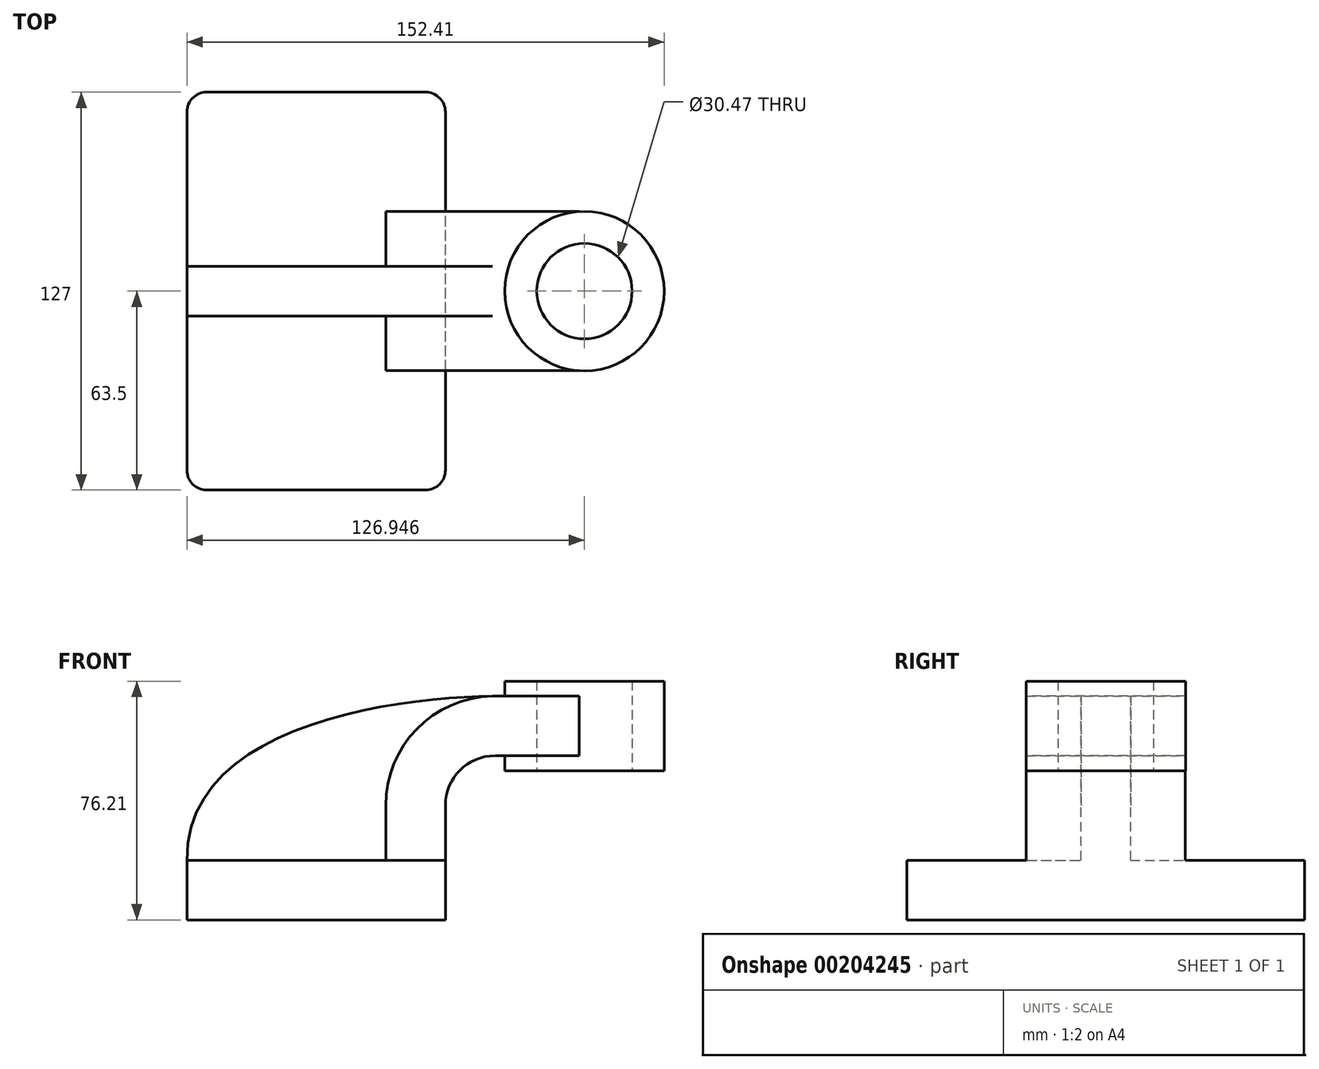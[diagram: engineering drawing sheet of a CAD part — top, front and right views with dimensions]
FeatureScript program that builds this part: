
annotation { "Feature Type Name" : "Feature", "Feature Type Description" : "" }
export const myFeature = defineFeature(function(context is Context, id is Id, definition is map)
    precondition{}
    {
        {
            var Q0;
            Q0=qCreatedBy(makeId("Front.planeOp"),FACE);
            var sketch = newSketch(context, id + "F0", { "sketchPlane" : qUnion([Q0])});
            skLineSegment(sketch, "E0.bottom", {"start": v(-41.28, -9.53) * mm, "end": v(41.28, -9.53) * mm});
            skLineSegment(sketch, "E0.top", {"start": v(-41.28, 9.53) * mm, "end": v(41.28, 9.53) * mm});
            skLineSegment(sketch, "E0.left", {"start": v(-41.28, -9.53) * mm, "end": v(-41.28, 9.53) * mm});
            skLineSegment(sketch, "E0.right", {"start": v(41.28, -9.53) * mm, "end": v(41.28, 9.52) * mm});
            skPoint(sketch, "E0.middle", {"position": v(0, 0) * mm});
            skLineSegment(sketch, "E1.bottom", {"start": v(60.33, 38.1) * mm, "end": v(111.12, 38.1) * mm});
            skLineSegment(sketch, "E1.top", {"start": v(60.33, 66.67) * mm, "end": v(111.12, 66.67) * mm});
            skLineSegment(sketch, "E1.left", {"start": v(60.33, 38.1) * mm, "end": v(60.33, 66.67) * mm});
            skLineSegment(sketch, "E1.right", {"start": v(111.12, 38.1) * mm, "end": v(111.12, 66.67) * mm});
            skPoint(sketch, "E1.middle", {"position": v(85.72, 52.39) * mm});
            skLineSegment(sketch, "E2", {"start": v(41.28, 9.53) * mm, "end": v(41.28, 27) * mm});
            skArc(sketch, "E3", {"start": v(41.27, 27) * mm, "mid": v(45.92, 38.23) * mm, "end": v(57.15, 42.88) * mm});
            skLineSegment(sketch, "E4", {"start": v(57.15, 42.88) * mm, "end": v(85.67, 42.88) * mm});
            skLineSegment(sketch, "E5.0", {"start": v(57.15, 61.93) * mm, "end": v(85.67, 61.93) * mm});
            skArc(sketch, "E5.1", {"start": v(22.23, 27) * mm, "mid": v(32.45, 51.7) * mm, "end": v(57.15, 61.93) * mm});
            skLineSegment(sketch, "E5.2", {"start": v(22.23, 9.53) * mm, "end": v(22.23, 27) * mm});
            skLineSegment(sketch, "E6", {"start": v(85.67, 66.67) * mm, "end": v(85.67, 38.1) * mm});
            skFitSpline(sketch, "E7", {"points": [v(-41.28, 9.53) * mm, v(57.15, 61.93) * mm], "startDerivative": vector(-1.17, 130.74) * mm, "endDerivative": vector(93.52, 0.92) * mm});
            skSolve(sketch);
        }
        {
            var Q0;
            Q0=makeQuery(id+"F0.imprint","IMPRINT",FACE,{"disambiguationData":[TD([[makeQuery(id+"F0.imprint","IMPRINT",EDGE,{"derivedFrom":sQuery(id+"F0.wireOp",EDGE,"E0.bottom")}),1.0]])]});
            extrude(context, id + "F1", {"entities" : qUnion([Q0]), "depth" : 127 * mm, "symmetric" : true});
        }
        {
            var Q0;
            {var subQ3=sQuery(id+"F0.wireOp",EDGE,"E5.2");Q0=makeQuery(id+"F0.imprint","IMPRINT",FACE,{"disambiguationData":[TD([[makeQuery(id+"F0.imprint","IMPRINT",EDGE,{"derivedFrom":subQ3}),1.0]])]});}
            extrude(context, id + "F2", {"entities" : qUnion([Q0]), "operationType" : NewBodyOperationType.ADD, "depth" : 15.88 * mm, "symmetric" : true});
        }
        {
            var Q0;
            {var subQ5=sQuery(id+"F0.wireOp",EDGE,"E2");Q0=makeQuery(id+"F0.imprint","IMPRINT",FACE,{"disambiguationData":[TD([[makeQuery(id+"F0.imprint","IMPRINT",EDGE,{"derivedFrom":subQ5}),1.0]])]});}
            var Q1;
            {var subQ0=sQuery(id+"F0.wireOp",EDGE,"E4");var subQ1=sQuery(id+"F0.wireOp",EDGE,"E1.left");var subQ2=makeQuery(id+"F0.imprint","INTERSECT",VERTEX,{"derivedFrom":[subQ1,subQ0]});Q1=makeQuery(id+"F0.imprint","IMPRINT",FACE,{"disambiguationData":[TD([[makeQuery(id+"F0.imprint","IMPRINT",EDGE,{"disambiguationData":[TD([[subQ2,-1.0]])],"derivedFrom":subQ1}),-1.0]])]});}
            extrude(context, id + "F3", {"entities" : qUnion([Q0, Q1]), "operationType" : NewBodyOperationType.ADD, "depth" : 50.8 * mm, "symmetric" : true});
        }
        {
            var Q0;
            {var subQ0=sQuery(id+"F0.wireOp",EDGE,"E1.right");Q0=makeQuery(id+"F0.imprint","IMPRINT",FACE,{"disambiguationData":[TD([[makeQuery(id+"F0.imprint","IMPRINT",EDGE,{"derivedFrom":subQ0}),1.0]])]});}
            var Q1;
            Q1=sQuery(id+"F0.wireOp",EDGE,"E6");
            revolve(context, id + "F4", {"operationType" : NewBodyOperationType.ADD, "entities" : qUnion([Q0]), "axis" : qUnion([Q1]), "revolveType" : RevolveType.FULL});
        }
        {
            var Q0;
            Q0=makeQuery(id+"F1.opExtrude","CAP_EDGE",EDGE,{"disambiguationData":[OSD([sQuery(id+"F0.wireOp",EDGE,"E0.left")])],"isStart":false});
            var Q1;
            Q1=makeQuery(id+"F1.opExtrude","CAP_EDGE",EDGE,{"disambiguationData":[OSD([sQuery(id+"F0.wireOp",EDGE,"E0.right")])],"isStart":false});
            var Q2;
            Q2=makeQuery(id+"F1.opExtrude","CAP_EDGE",EDGE,{"disambiguationData":[OSD([sQuery(id+"F0.wireOp",EDGE,"E0.right")])],"isStart":true});
            var Q3;
            Q3=makeQuery(id+"F1.opExtrude","CAP_EDGE",EDGE,{"disambiguationData":[OSD([sQuery(id+"F0.wireOp",EDGE,"E0.left")])],"isStart":true});
            fillet(context, id + "F5", {"entities" : qUnion([Q0, Q1, Q2, Q3]), "radius" : 6.35 * mm, "tangentPropagation" : true, "allowEdgeOverflow" : false});
        }
        {
            var Q0;
            Q0=makeQuery(id+"F4.opRevolve","SWEPT_FACE",FACE,{"disambiguationData":[OSD([sQuery(id+"F0.wireOp",EDGE,"E1.bottom")])]});
            var sketch = newSketch(context, id + "F6", { "sketchPlane" : qUnion([Q0])});
            skCircle(sketch, "E8", {"center": v(85.67, 0) * mm, "radius": 15.24 * mm});
            skCircle(sketch, "E9.0", {"center": v(85.67, 0) * mm, "radius": 25.46 * mm});
            skSolve(sketch);
        }
        {
            var Q0;
            Q0=makeQuery(id+"F6.imprint","IMPRINT",FACE,{"disambiguationData":[TD([[makeQuery(id+"F6.imprint","IMPRINT",EDGE,{"derivedFrom":sQuery(id+"F6.wireOp",EDGE,"E8")}),1.0]])]});
            extrude(context, id + "F7", {"entities" : qUnion([Q0]), "operationType" : NewBodyOperationType.REMOVE, "oppositeDirection" : true, "depth" : 28.57 * mm});
        }
    });
